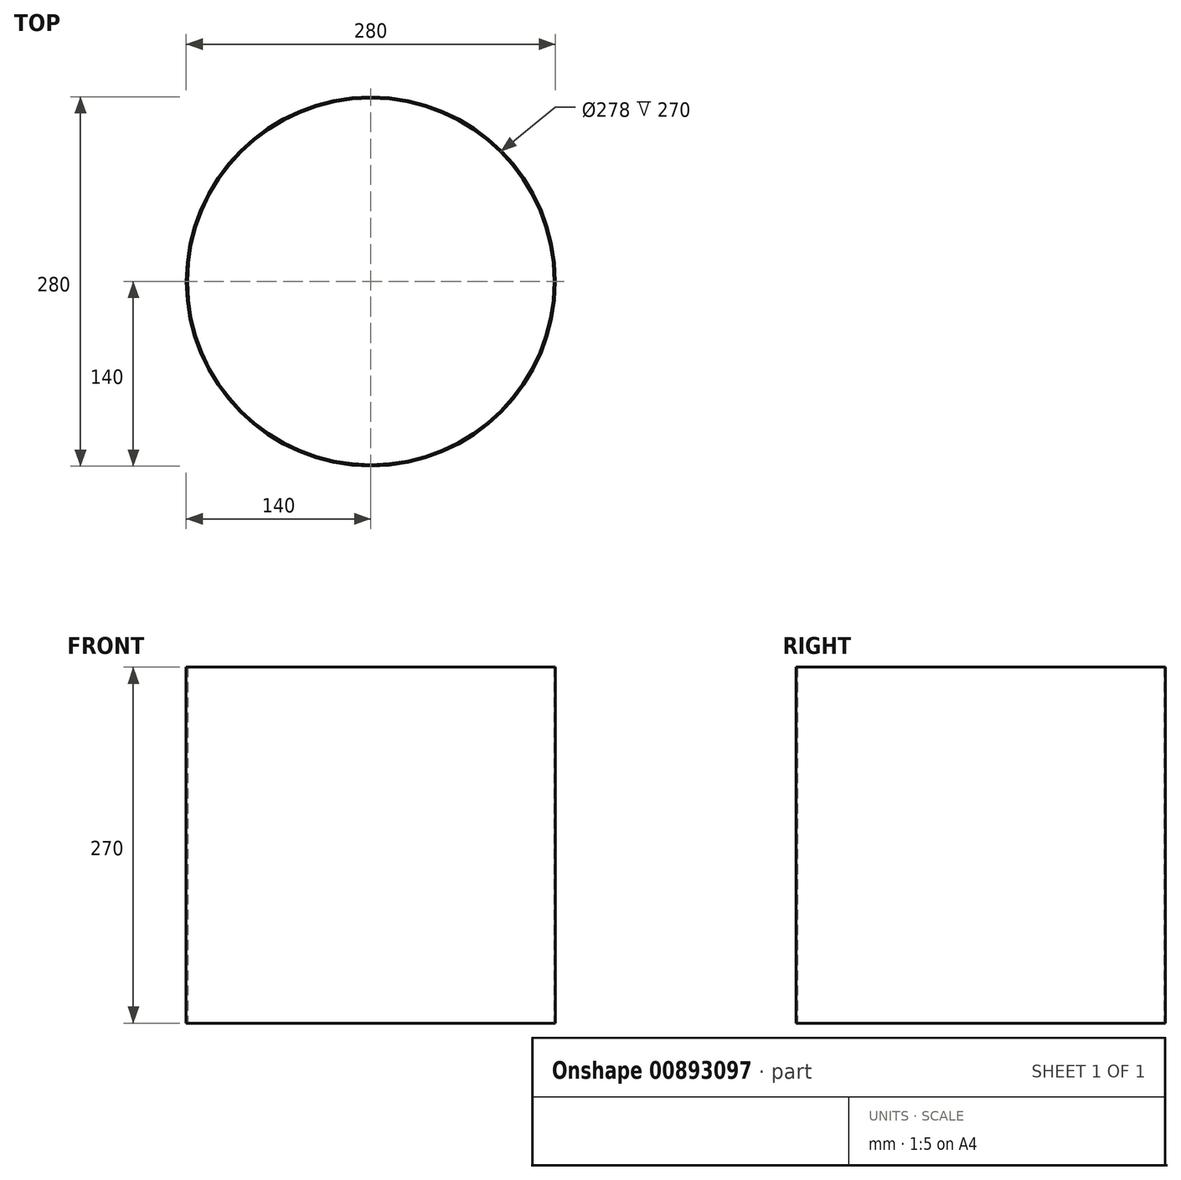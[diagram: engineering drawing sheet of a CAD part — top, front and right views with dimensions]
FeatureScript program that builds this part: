
annotation { "Feature Type Name" : "Feature", "Feature Type Description" : "" }
export const myFeature = defineFeature(function(context is Context, id is Id, definition is map)
    precondition{}
    {
        {
            var Q0;
            Q0=qCreatedBy(makeId("Top.planeOp"),FACE);
            var sketch = newSketch(context, id + "F0", { "sketchPlane" : qUnion([Q0])});
            skCircle(sketch, "E0", {"center": v(0, 0) * mm, "radius": 140 * mm});
            skCircle(sketch, "E1", {"center": v(0, 0) * mm, "radius": 139 * mm});
            skSolve(sketch);
        }
        {
            var Q0;
            Q0=makeQuery(id+"F0.imprint","IMPRINT",FACE,{"disambiguationData":[TD([[makeQuery(id+"F0.imprint","IMPRINT",EDGE,{"derivedFrom":sQuery(id+"F0.wireOp",EDGE,"E0")}),1.0]])]});
            extrude(context, id + "F1", {"entities" : qUnion([Q0]), "depth" : 270 * mm, "offsetDistance" : 25 * mm});
        }
    });
